# Revit family: Legrand_Coffrets HYPRA équipés 3 prises IP44 avec disjoncteur + interdifférentiel + transformateur
name_source: partatom
category: Equipement électrique
units: mm (PartAtom-declared; Revit-internal decimal feet)

## family parameters
Basée sur le plan de construction = Non
Configuration du panneau = Deux colonnes, circuits au sein
Cote de connecteur circulaire = Utiliser le diamètre
Couper avec des vides une fois chargée = Non
Numéro OmniClass = 23.80.30.11.17
Partagée = Non
Point de calcul de pièce = Non
Titre OmniClass = Distribution Boards and Control Panels
Toujours verticalement = Oui
Type d'élément = Tableau de raccordement

## types (1)
- Référence 059861
    Classe de protection = IP44
    Conditions Générale d'Utilisation = https://export.legrand.com
    Description = Coffret multiprise Hypra équipé
    Elévation par défaut = 0 mm  [stored 0 ft]
    Fabricant = Legrand
    IEC 61439-2 = 20A
    IEC 61439-3 = 20A
    Modèle = Référence 059861
    Nombre de prise 2P = 1 tension 20 à 25 V
    Nombre de prise 2P+T 16A = 1 tension 200 à 250 V
    Nombre de prise 2P+T NFC 16A = 1 tension 200 à 250 V
    Protection = Disjoncteur + interdifférentiel
    Transformateur = 100VA
    URL = www.legrand.fr

note: [stored X ft] marks values corroborated as IEEE doubles in the binary element streams (Revit-internal decimal feet)
